# Revit family: BFP-WPL-DSD-MS-___
name_source: partatom
category: Electrical Equipment
revit_build: Autodesk Revit 2018 (Build: 20170223_1515(x64)
units: mm (PartAtom-declared; Revit-internal decimal feet)

## family parameters
Cut with Voids When Loaded = No
Host = Face
OmniClass Number = 23.29.31.13.13
OmniClass Title = Secondary Fire Alarm Control Panels
Part Type = Other Panel
Room Calculation Point = No
Round Connector Dimension = Use Diameter
Shared = No

## types (2) — shared parameters
DSD.Com.CAT Code = BFP
Default Elevation = 1219 mm
Panel Small R = 20 mm  [stored 0.0656168 ft]
r = 40 mm  [stored 0.131234 ft]
zero-valued in all types: DSD.BFP.Height, DSD.BFP.Length, DSD.BFP.Width

## per-type parameters (varying)
| type | H | H2 | H3 | H4 | High | L1 | Panel H1 | Panel Thick | Thick | W | Width | void1 | void1 h e | void1 h s |
| 2/4/8/16 Zone | 569 mm | 170 mm  [stored 0.557743 ft] | 20 mm  [stored 0.0656168 ft] | 45 mm  [stored 0.147638 ft] | 370 mm  [stored 1.21391 ft] | 20 mm  [stored 0.0656168 ft] | 300 mm  [stored 0.984252 ft] | 128 mm  [stored 0.419948 ft] | 126 mm  [stored 0.413386 ft] | 525 mm | 325 mm  [stored 1.06627 ft] | 328 mm  [stored 1.07612 ft] | 126 mm  [stored 0.413386 ft] | 124 mm  [stored 0.406824 ft] |
| 32 Zone | 640 mm  [stored 2.09974 ft] | 210 mm | 25 mm  [stored 0.082021 ft] | 56 mm | 441 mm  [stored 1.44685 ft] | 25 mm  [stored 0.082021 ft] | 371 mm  [stored 1.21719 ft] | 133 mm  [stored 0.436352 ft] | 131 mm  [stored 0.42979 ft] | 600 mm | 400 mm  [stored 1.31234 ft] | 399 mm  [stored 1.30906 ft] | 131 mm  [stored 0.42979 ft] | 129 mm  [stored 0.423228 ft] |

note: [stored X ft] marks values corroborated as IEEE doubles in the binary element streams (Revit-internal decimal feet)

## geometry (parser evidence)
native form markers: Blend x4, Sweep x8
no freeform markers — native parametric forms only
